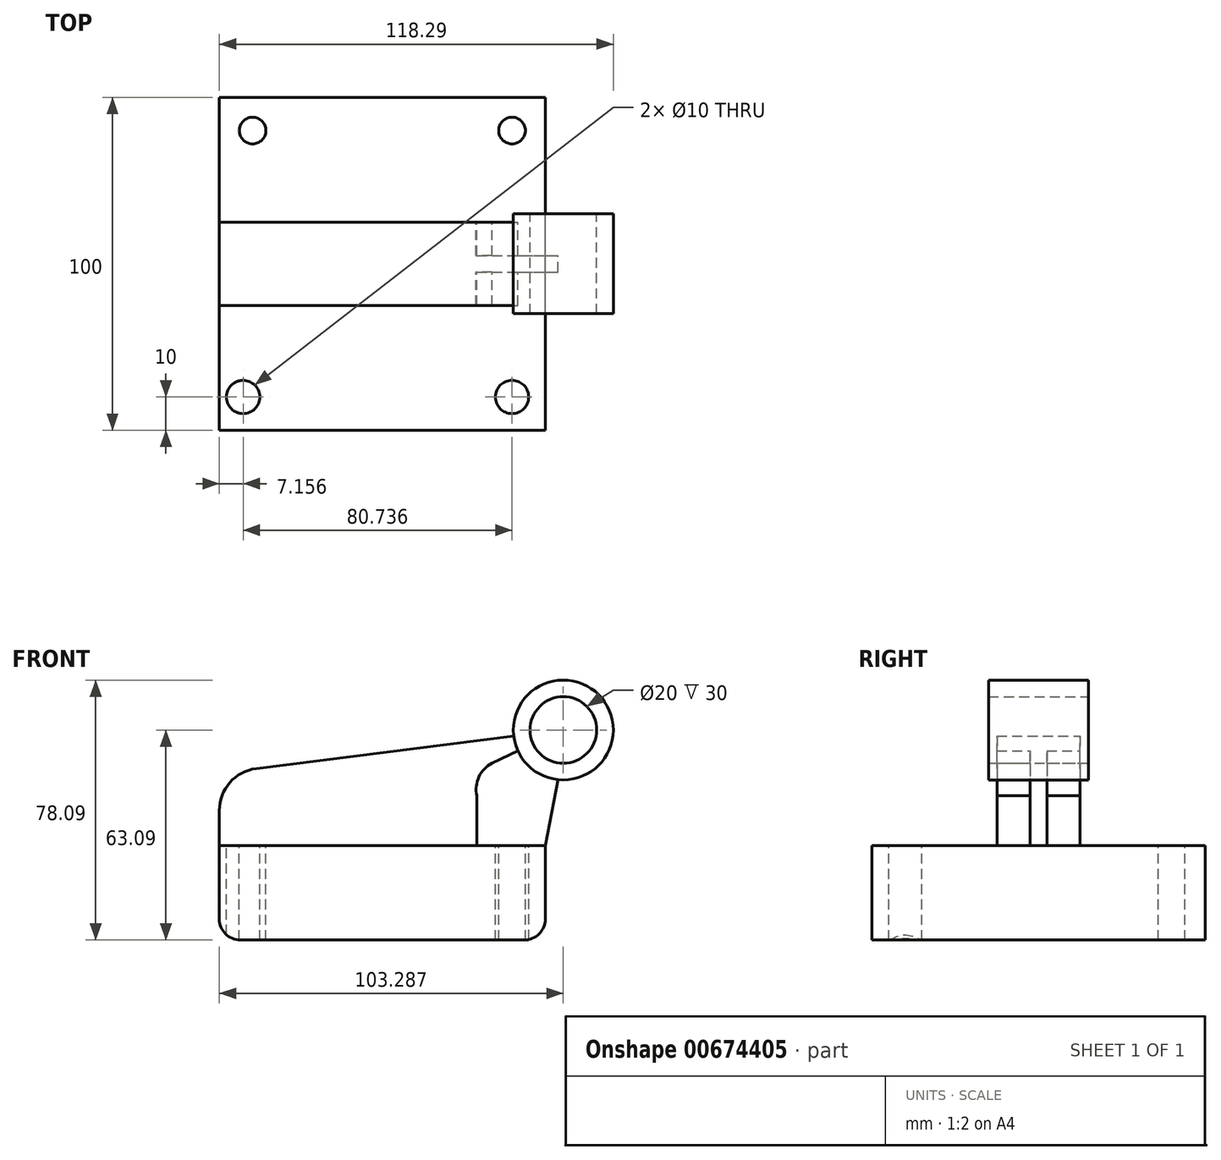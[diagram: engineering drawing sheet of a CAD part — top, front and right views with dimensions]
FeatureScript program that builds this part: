
annotation { "Feature Type Name" : "Feature", "Feature Type Description" : "" }
export const myFeature = defineFeature(function(context is Context, id is Id, definition is map)
    precondition{}
    {
        {
            var Q0;
            Q0=qCreatedBy(makeId("Front.planeOp"),FACE);
            var sketch = newSketch(context, id + "F0", { "sketchPlane" : qUnion([Q0])});
            skLineSegment(sketch, "E0.bottom", {"start": v(-46.5, 14.37) * mm, "end": v(51.4, 14.37) * mm});
            skLineSegment(sketch, "E0.top", {"start": v(-40.15, -14) * mm, "end": v(45.04, -14) * mm});
            skLineSegment(sketch, "E0.left", {"start": v(-46.5, 14.37) * mm, "end": v(-46.5, -7.64) * mm});
            skLineSegment(sketch, "E0.right", {"start": v(51.4, 14.37) * mm, "end": v(51.4, -7.64) * mm});
            skCircle(sketch, "E1", {"center": v(56.79, 49.1) * mm, "radius": 15 * mm});
            skPoint(sketch, "E2.visualSharp", {"position": v(51.4, -14) * mm});
            skArc(sketch, "E2.filletArc", {"start": v(45.04, -14) * mm, "mid": v(49.53, -12.13) * mm, "end": v(51.4, -7.64) * mm});
            skPoint(sketch, "E3.visualSharp", {"position": v(-46.5, -14) * mm});
            skArc(sketch, "E3.filletArc", {"start": v(-46.5, -7.64) * mm, "mid": v(-44.64, -12.13) * mm, "end": v(-40.15, -14) * mm});
            skLineSegment(sketch, "E4", {"start": v(30.84, 14.37) * mm, "end": v(30.84, 31.3) * mm});
            skArc(sketch, "E5", {"start": v(35.42, 39.18) * mm, "mid": v(31.44, 35.03) * mm, "end": v(30.84, 29.3) * mm});
            skLineSegment(sketch, "E6", {"start": v(35.42, 39.18) * mm, "end": v(56.79, 49.1) * mm});
            skLineSegment(sketch, "E7", {"start": v(-46.5, 14.37) * mm, "end": v(-46.5, 24.92) * mm});
            skLineSegment(sketch, "E8", {"start": v(-35.38, 37.52) * mm, "end": v(56.79, 49.1) * mm});
            skPoint(sketch, "E9.visualSharp", {"position": v(-46.5, 36.13) * mm});
            skArc(sketch, "E9.filletArc", {"start": v(-35.38, 37.52) * mm, "mid": v(-43.32, 33.32) * mm, "end": v(-46.5, 24.92) * mm});
            skLineSegment(sketch, "E10", {"start": v(51.4, 14.37) * mm, "end": v(55.2, 34.18) * mm});
            skCircle(sketch, "E11.0", {"center": v(56.79, 49.1) * mm, "radius": 10 * mm});
            skSolve(sketch);
        }
        {
            var Q0;
            Q0=makeQuery(id+"F0.imprint","IMPRINT",FACE,{"disambiguationData":[TD([[makeQuery(id+"F0.imprint","IMPRINT",EDGE,{"derivedFrom":sQuery(id+"F0.wireOp",EDGE,"E0.top")}),1.0]])]});
            extrude(context, id + "F1", {"entities" : qUnion([Q0]), "endBound" : BoundingType.SYMMETRIC, "depth" : 100 * mm, "offsetDistance" : 25 * mm});
        }
        {
            var Q0;
            {var subQ0=sQuery(id+"F0.wireOp",EDGE,"E5");Q0=makeQuery(id+"F0.imprint","IMPRINT",FACE,{"disambiguationData":[TD([[makeQuery(id+"F0.imprint","IMPRINT",EDGE,{"derivedFrom":subQ0}),-1.0]])]});}
            extrude(context, id + "F2", {"entities" : qUnion([Q0]), "operationType" : NewBodyOperationType.ADD, "endBound" : BoundingType.SYMMETRIC, "depth" : 25 * mm, "offsetDistance" : 25 * mm});
        }
        {
            var Q0;
            {var subQ3=sQuery(id+"F0.wireOp",EDGE,"E5");Q0=makeQuery(id+"F0.imprint","IMPRINT",FACE,{"disambiguationData":[TD([[makeQuery(id+"F0.imprint","IMPRINT",EDGE,{"derivedFrom":subQ3}),1.0]])]});}
            extrude(context, id + "F3", {"entities" : qUnion([Q0]), "operationType" : NewBodyOperationType.ADD, "endBound" : BoundingType.SYMMETRIC, "depth" : 5 * mm, "offsetDistance" : 25 * mm});
        }
        {
            var Q0;
            {var subQ0=sQuery(id+"F0.wireOp",EDGE,"E8");var subQ1=sQuery(id+"F0.wireOp",EDGE,"E1");var subQ2=makeQuery(id+"F0.imprint","INTERSECT",VERTEX,{"derivedFrom":[subQ1,subQ0]});Q0=makeQuery(id+"F0.imprint","IMPRINT",FACE,{"disambiguationData":[TD([[makeQuery(id+"F0.imprint","IMPRINT",EDGE,{"disambiguationData":[TD([[subQ2,-1.0]])],"derivedFrom":subQ1}),1.0]])]});}
            var Q1;
            Q1=sQuery(id+"F0.wireOp",EDGE,"E1");
            extrude(context, id + "F4", {"entities" : qUnion([Q0]), "operationType" : NewBodyOperationType.ADD, "surfaceEntities" : qUnion([Q1]), "endBound" : BoundingType.SYMMETRIC, "depth" : 30 * mm, "offsetDistance" : 25 * mm});
        }
        {
            var Q0;
            {var subQ0=sQuery(id+"F0.wireOp",EDGE,"E1");var subQ1=makeQuery(id+"F0.imprint","INTERSECT",VERTEX,{"derivedFrom":[subQ0,sQuery(id+"F0.wireOp",EDGE,"E10")]});Q0=makeQuery(id+"F0.imprint","IMPRINT",FACE,{"disambiguationData":[TD([[makeQuery(id+"F0.imprint","IMPRINT",EDGE,{"disambiguationData":[TD([[subQ1,1.0]])],"derivedFrom":subQ0}),1.0]])]});}
            extrude(context, id + "F5", {"entities" : qUnion([Q0]), "operationType" : NewBodyOperationType.ADD, "endBound" : BoundingType.SYMMETRIC, "depth" : 30 * mm, "offsetDistance" : 25 * mm});
        }
        {
            var Q0;
            {var subQ5=sQuery(id+"F0.wireOp",EDGE,"E0.bottom");var subQ6=sQuery(id+"F0.wireOp",EDGE,"E0.right");var subQ7=sQuery(id+"F0.wireOp",EDGE,"E0.left");Q0=makeQuery(id+"F3.boolean.opBoolean","SPLIT",FACE,{"disambiguationData":[TD([makeQuery(id+"F1.opExtrude","CAP_FACE",FACE,{"disambiguationData":[OSD([subQ5,sQuery(id+"F0.wireOp",EDGE,"E0.top"),subQ7,subQ6,sQuery(id+"F0.wireOp",EDGE,"E2.filletArc"),sQuery(id+"F0.wireOp",EDGE,"E3.filletArc")])],"isStart":true})])],"derivedFrom":makeQuery(id+"F1.opExtrude","SWEPT_FACE",FACE,{"disambiguationData":[OSD([subQ5])]})});}
            var sketch = newSketch(context, id + "F6", { "sketchPlane" : qUnion([Q0])});
            skCircle(sketch, "E12", {"center": v(-36.5, 40) * mm, "radius": 4 * mm});
            skCircle(sketch, "E13", {"center": v(41.4, 40) * mm, "radius": 4 * mm});
            skCircle(sketch, "E14", {"center": v(-39.34, -40) * mm, "radius": 5 * mm});
            skCircle(sketch, "E15", {"center": v(41.4, -40) * mm, "radius": 5 * mm});
            skSolve(sketch);
        }
        {
            var Q0;
            Q0 = qSketchRegion(id + "F6", true);
            extrude(context, id + "F7", {"entities" : qUnion([Q0]), "operationType" : NewBodyOperationType.REMOVE, "endBound" : BoundingType.UP_TO_NEXT, "oppositeDirection" : true, "depth" : 25 * mm, "offsetDistance" : 25 * mm});
        }
    });
